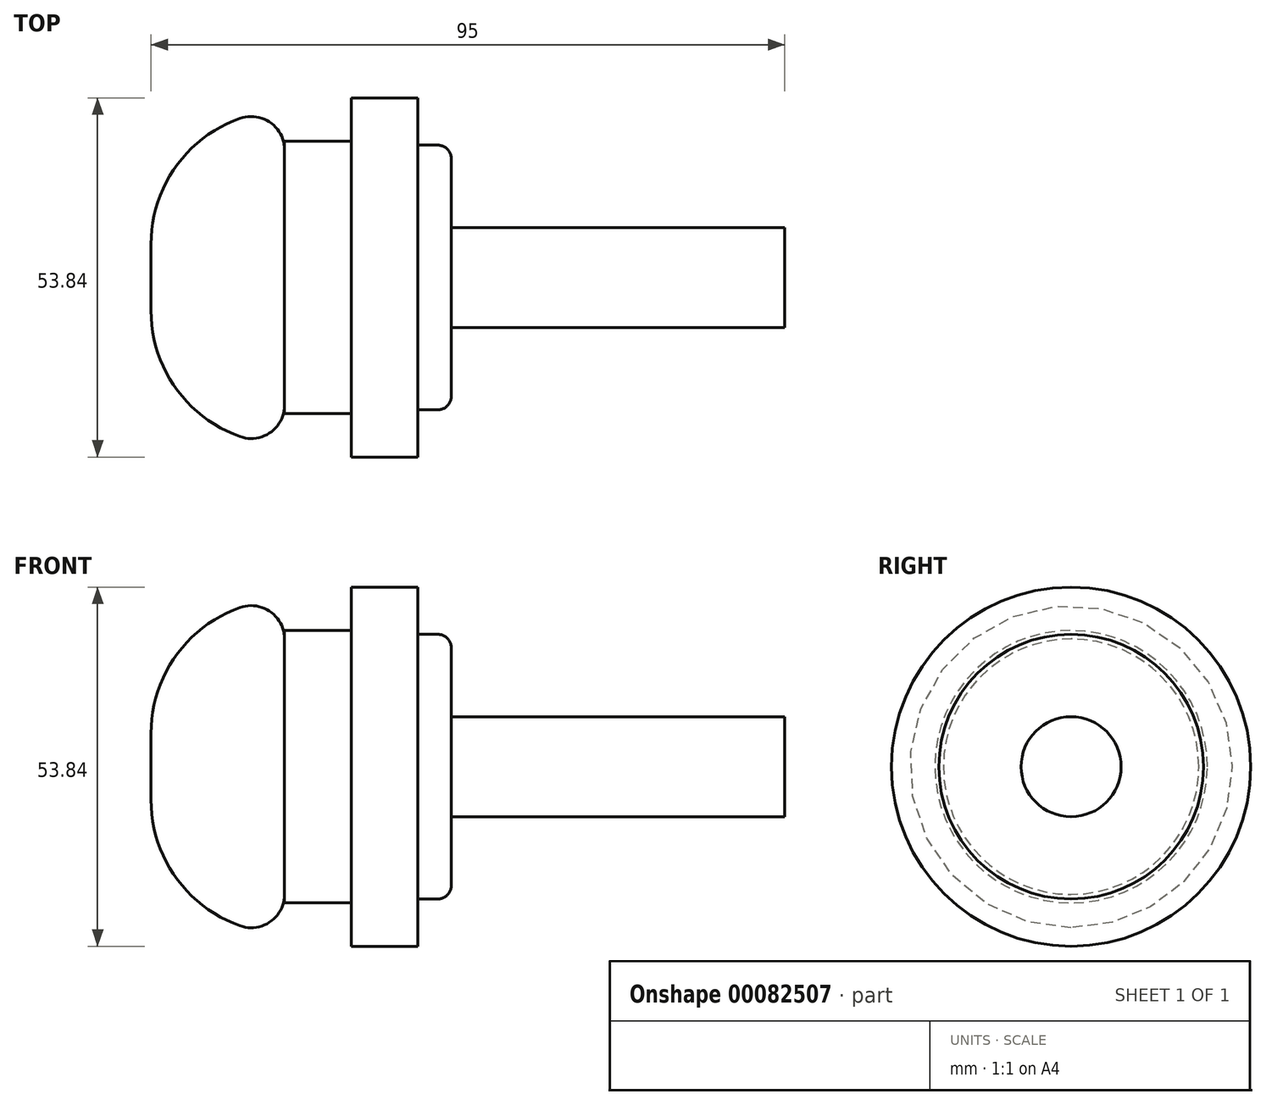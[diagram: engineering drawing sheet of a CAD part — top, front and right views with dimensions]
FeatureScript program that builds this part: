
annotation { "Feature Type Name" : "Feature", "Feature Type Description" : "" }
export const myFeature = defineFeature(function(context is Context, id is Id, definition is map)
    precondition{}
    {
        {
            var Q0;
            Q0=qCreatedBy(makeId("Right.planeOp"),FACE);
            var sketch = newSketch(context, id + "F0", { "sketchPlane" : qUnion([Q0])});
            skCircle(sketch, "E0", {"center": v(0, 0) * mm, "radius": 25 * mm});
            skSolve(sketch);
        }
        {
            var Q0;
            Q0=qSketchRegion(id+"F0",true);
            extrude(context, id + "F1", {"entities" : qUnion([Q0]), "depth" : 20 * mm});
        }
        {
            var Q0;
            Q0=makeQuery(id+"F1.opExtrude","CAP_EDGE",EDGE,{"disambiguationData":[OSD([sQuery(id+"F0.wireOp",EDGE,"E0")])],"isStart":true});
            fillet(context, id + "F2", {"entities" : qUnion([Q0]), "radius" : 20 * mm, "tangentPropagation" : true, "allowEdgeOverflow" : false});
        }
        {
            var Q0;
            Q0=makeQuery(id+"F1.opExtrude","CAP_FACE",FACE,{"disambiguationData":[OSD([sQuery(id+"F0.wireOp",EDGE,"E0")])],"isStart":false});
            fillet(context, id + "F3", {"entities" : qUnion([Q0]), "radius" : 5 * mm, "tangentPropagation" : true, "allowEdgeOverflow" : false});
        }
        {
            var Q0;
            Q0=makeQuery(id+"F1.opExtrude","CAP_FACE",FACE,{"disambiguationData":[OSD([sQuery(id+"F0.wireOp",EDGE,"E0")])],"isStart":false});
            var sketch = newSketch(context, id + "F4", { "sketchPlane" : qUnion([Q0])});
            skCircle(sketch, "E1", {"center": v(0, 0) * mm, "radius": 20.42 * mm});
            skSolve(sketch);
        }
        {
            var Q0;
            Q0=qSketchRegion(id+"F4",true);
            extrude(context, id + "F5", {"entities" : qUnion([Q0]), "operationType" : NewBodyOperationType.ADD, "depth" : 10 * mm});
        }
        {
            var Q0;
            Q0=makeQuery(id+"F5.opExtrude","CAP_FACE",FACE,{"disambiguationData":[OSD([sQuery(id+"F4.wireOp",EDGE,"E1")])],"isStart":false});
            var sketch = newSketch(context, id + "F6", { "sketchPlane" : qUnion([Q0])});
            skCircle(sketch, "E2", {"center": v(0, 0) * mm, "radius": 26.92 * mm});
            skSolve(sketch);
        }
        {
            var Q0;
            Q0=qSketchRegion(id+"F6",true);
            extrude(context, id + "F7", {"entities" : qUnion([Q0]), "operationType" : NewBodyOperationType.ADD, "depth" : 10 * mm});
        }
        {
            var Q0;
            Q0=makeQuery(id+"F7.opExtrude","CAP_FACE",FACE,{"disambiguationData":[OSD([sQuery(id+"F6.wireOp",EDGE,"E2")])],"isStart":false});
            var sketch = newSketch(context, id + "F8", { "sketchPlane" : qUnion([Q0])});
            skCircle(sketch, "E3", {"center": v(0, 0) * mm, "radius": 19.84 * mm});
            skSolve(sketch);
        }
        {
            var Q0;
            Q0=makeQuery(id+"F8.imprint","IMPRINT",FACE,{"disambiguationData":[TD([[makeQuery(id+"F8.imprint","IMPRINT",EDGE,{"derivedFrom":sQuery(id+"F8.wireOp",EDGE,"E3")}),1.0]])]});
            extrude(context, id + "F9", {"entities" : qUnion([Q0]), "operationType" : NewBodyOperationType.ADD, "depth" : 5 * mm});
        }
        {
            var Q0;
            Q0=makeQuery(id+"F9.opExtrude","CAP_EDGE",EDGE,{"disambiguationData":[OSD([sQuery(id+"F8.wireOp",EDGE,"E3")])],"isStart":false});
            fillet(context, id + "F10", {"entities" : qUnion([Q0]), "radius" : 2 * mm, "tangentPropagation" : true, "allowEdgeOverflow" : false});
        }
        {
            var Q0;
            Q0=makeQuery(id+"F9.opExtrude","CAP_FACE",FACE,{"disambiguationData":[OSD([sQuery(id+"F8.wireOp",EDGE,"E3")])],"isStart":false});
            var sketch = newSketch(context, id + "F11", { "sketchPlane" : qUnion([Q0])});
            skCircle(sketch, "E4", {"center": v(0, 0) * mm, "radius": 7.5 * mm});
            skSolve(sketch);
        }
        {
            var Q0;
            Q0=makeQuery(id+"F11.imprint","IMPRINT",FACE,{"disambiguationData":[TD([[makeQuery(id+"F11.imprint","IMPRINT",EDGE,{"derivedFrom":sQuery(id+"F11.wireOp",EDGE,"E4")}),1.0]])]});
            extrude(context, id + "F12", {"entities" : qUnion([Q0]), "operationType" : NewBodyOperationType.ADD, "depth" : 50 * mm});
        }
    });
